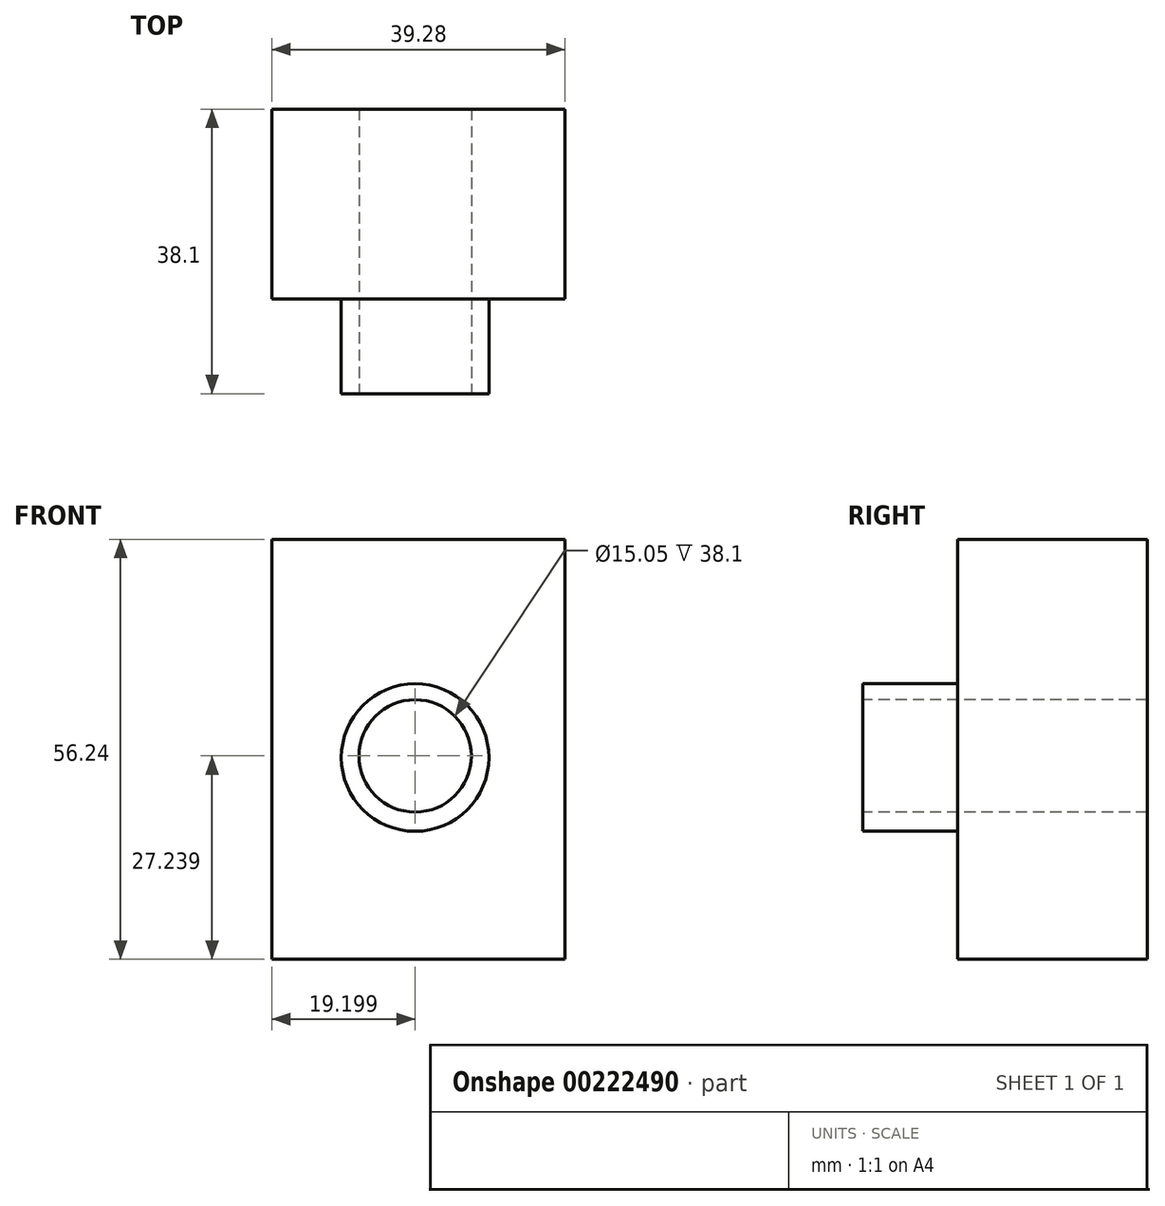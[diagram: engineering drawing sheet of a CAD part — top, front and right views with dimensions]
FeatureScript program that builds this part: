
annotation { "Feature Type Name" : "Feature", "Feature Type Description" : "" }
export const myFeature = defineFeature(function(context is Context, id is Id, definition is map)
    precondition{}
    {
        {
            var Q0;
            Q0=qCreatedBy(makeId("Front.planeOp"),FACE);
            var sketch = newSketch(context, id + "F0", { "sketchPlane" : qUnion([Q0])});
            skLineSegment(sketch, "E0.bottom", {"start": v(-29.6, -6.76) * mm, "end": v(9.7, -6.76) * mm});
            skLineSegment(sketch, "E0.top", {"start": v(-29.6, 49.48) * mm, "end": v(9.7, 49.48) * mm});
            skLineSegment(sketch, "E0.left", {"start": v(-29.6, -6.76) * mm, "end": v(-29.6, 49.48) * mm});
            skLineSegment(sketch, "E0.right", {"start": v(9.7, -6.76) * mm, "end": v(9.7, 49.48) * mm});
            skSolve(sketch);
        }
        {
            var Q0;
            Q0 = qSketchRegion(id + "F0", true);
            extrude(context, id + "F1", {"entities" : qUnion([Q0]), "depth" : 25.4 * mm});
        }
        {
            var Q0;
            Q0=makeQuery(id+"F1.opExtrude","CAP_FACE",FACE,{"disambiguationData":[OSD([sQuery(id+"F0.wireOp",EDGE,"E0.bottom"),sQuery(id+"F0.wireOp",EDGE,"E0.top"),sQuery(id+"F0.wireOp",EDGE,"E0.left"),sQuery(id+"F0.wireOp",EDGE,"E0.right")])],"isStart":false});
            var sketch = newSketch(context, id + "F2", { "sketchPlane" : qUnion([Q0])});
            skCircle(sketch, "E1", {"center": v(-10.4, 20.26) * mm, "radius": 9.88 * mm});
            skSolve(sketch);
        }
        {
            var Q0;
            Q0=makeQuery(id+"F2.imprint","IMPRINT",FACE,{"disambiguationData":[TD([[makeQuery(id+"F2.imprint","IMPRINT",EDGE,{"derivedFrom":sQuery(id+"F2.wireOp",EDGE,"E1")}),1.0]])]});
            extrude(context, id + "F3", {"entities" : qUnion([Q0]), "operationType" : NewBodyOperationType.ADD, "depth" : 12.7 * mm});
        }
        {
            var Q0;
            Q0=makeQuery(id+"F3.opExtrude","CAP_FACE",FACE,{"disambiguationData":[OSD([sQuery(id+"F2.wireOp",EDGE,"E1")])],"isStart":false});
            var sketch = newSketch(context, id + "F4", { "sketchPlane" : qUnion([Q0])});
            skSolve(sketch);
        }
        {
            var Q0;
            Q0=makeQuery(id+"F4.imprint","IMPRINT",FACE,{"disambiguationData":[TD([[makeQuery(id+"F4.imprint","IMPRINT",EDGE,{"derivedFrom":makeQuery(id+"F3.opExtrude","CAP_EDGE",EDGE,{"disambiguationData":[OSD([sQuery(id+"F2.wireOp",EDGE,"E1")])],"isStart":false})}),1.0]])]});
            var sketch = newSketch(context, id + "F5", { "sketchPlane" : qUnion([Q0])});
            skCircle(sketch, "E2", {"center": v(-10.4, 20.48) * mm, "radius": 7.52 * mm});
            skSolve(sketch);
        }
        {
            var Q0;
            Q0 = qSketchRegion(id + "F5", true);
            extrude(context, id + "F6", {"entities" : qUnion([Q0]), "operationType" : NewBodyOperationType.REMOVE, "endBound" : BoundingType.THROUGH_ALL, "oppositeDirection" : true, "depth" : 25.4 * mm});
        }
    });
